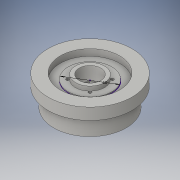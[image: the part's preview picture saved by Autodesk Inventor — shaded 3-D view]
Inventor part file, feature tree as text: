
AUTODESK INVENTOR PART (.ipt)
format: ipt  version: 2016 (Build 200138000, 138)  size: 180,736 bytes
history: native  units: in
note: dims shown in document units (in); Inventor stores cm internally (conversion verified against a paired STEP export)
features: sketch x8, extrude x7, hole x1
ambient origin geometry x8: Origin, YZ Plane, XZ Plane, XY Plane, X Axis, Y Axis, Z Axis, Center Point
bodies: Solid1 (feature_tree)
feature tree (16):
  extrude  "Extrusion1"  Depth=0.6299in TaperAngle=0.0deg
  extrude  "Extrusion2"  Depth=0.3543in TaperAngle=0.0deg
  extrude  "Extrusion3"  Depth=0.9843in TaperAngle=0.0deg
  sketch  "Sketch4"  dims[d9=2.3622in d10=0.0512in d11=0.0in]
  extrude  "Extrusion4"  Depth=0.0512in TaperAngle=0.0deg
  extrude  "Extrusion5"  Depth=0.2362in TaperAngle=0.0deg
  extrude  "Extrusion6"  Depth=1.9685in TaperAngle=0.0deg
  sketch  "Sketch8"  dims[d18=0.7874in d19=0.0in d34=0.8661in]
  extrude  "Extrusion7"  Depth=0.7874in
  hole  "Hole5"  [1 undecoded]
  sketch  "Sketch1"  dims[d0=4.5669in d1=0.6299in d2=0.0in]
  sketch  "Sketch2"  dims[d3=3.2283in d4=0.3543in d5=0.0in]
  sketch  "Sketch3"  dims[d6=3.937in d7=0.9843in d8=0.0in]
  sketch  "Sketch6"  dims[d12=1.5748in d13=0.2362in d14=0.0in]
  sketch  "Sketch7"  dims[d15=1.1811in d16=1.9685in d17=0.0in]
  sketch  "Sketch12"  dims[d35=0.8661in d36=0.8661in d37=0.8661in d72=1.2205in d73=1.2205in d74=1.2205in d75=1.2205in d76=0.6102in d77=0.6102in d78=0.1181in d79=0.2362in d80=0.1575in d81=0.0787in d82=90.0deg d83=0.315in d84=0.8108in d85=0.6102in]
note: 1 required parameter value undecoded (feature->parameter linkage not recoverable at this tier; creation-order binding heuristic only, values carry confidence <= 0.55)
